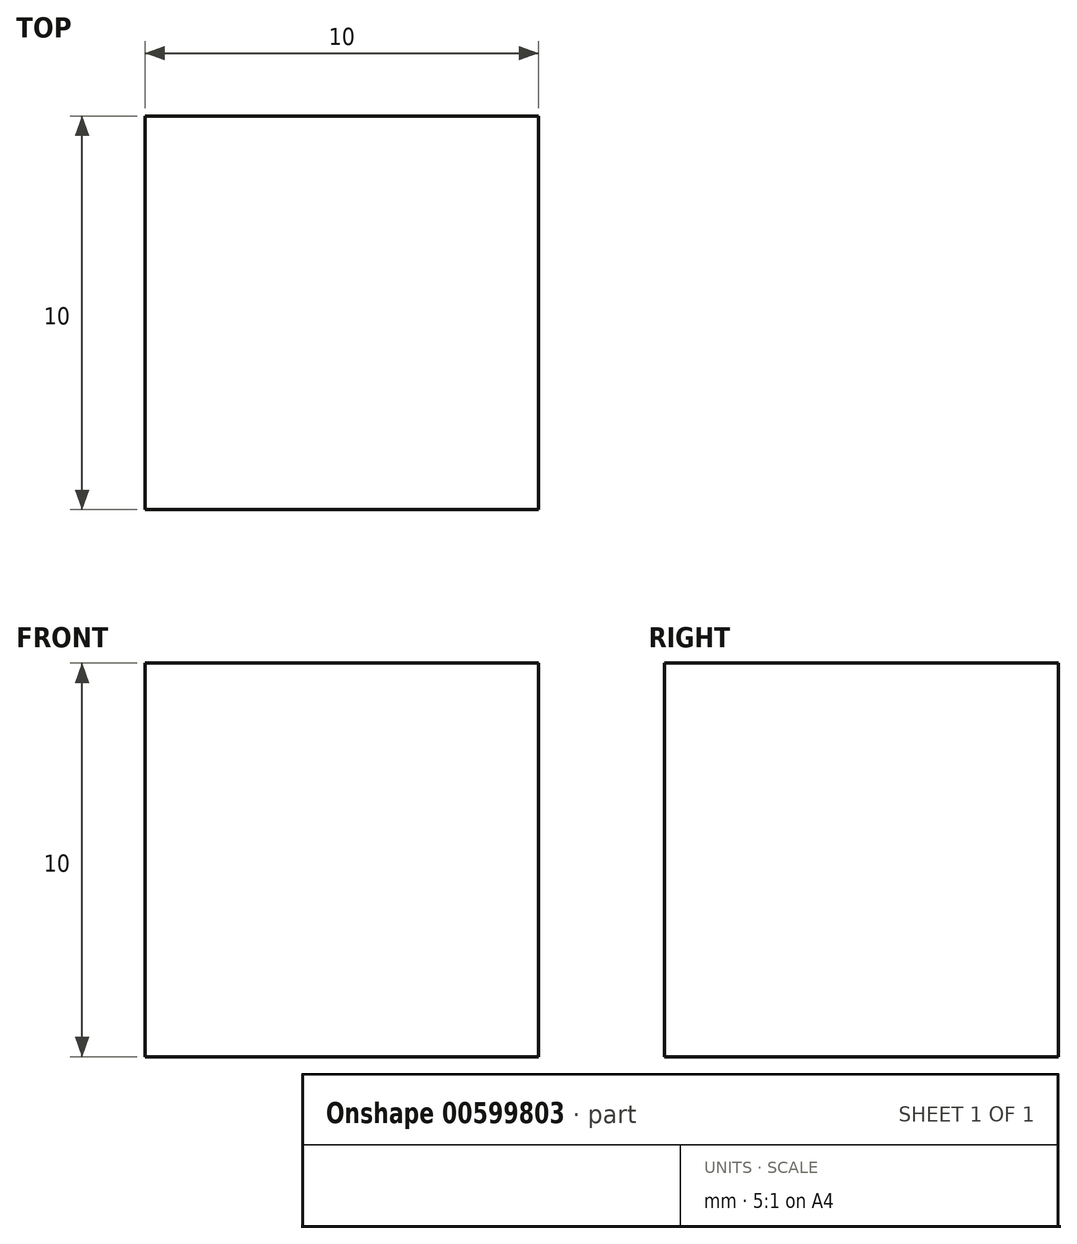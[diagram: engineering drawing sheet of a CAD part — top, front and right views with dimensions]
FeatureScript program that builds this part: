
annotation { "Feature Type Name" : "Feature", "Feature Type Description" : "" }
export const myFeature = defineFeature(function(context is Context, id is Id, definition is map)
    precondition{}
    {
        {
            var Q0;
            Q0=qCreatedBy(makeId("Top.planeOp"),FACE);
            var sketch = newSketch(context, id + "F0", { "sketchPlane" : qUnion([Q0])});
            skLineSegment(sketch, "E0.bottom", {"start": v(-98.38, 4.07) * mm, "end": v(-88.38, 4.07) * mm});
            skLineSegment(sketch, "E0.top", {"start": v(-98.38, -5.93) * mm, "end": v(-88.38, -5.93) * mm});
            skLineSegment(sketch, "E0.left", {"start": v(-98.38, 4.07) * mm, "end": v(-98.38, -5.93) * mm});
            skLineSegment(sketch, "E0.right", {"start": v(-88.38, 4.07) * mm, "end": v(-88.38, -5.93) * mm});
            skSolve(sketch);
        }
        {
            var Q0;
            Q0 = qSketchRegion(id + "F0", true);
            extrude(context, id + "F1", {"entities" : qUnion([Q0]), "depth" : 10 * mm, "offsetDistance" : 25 * mm});
        }
    });
